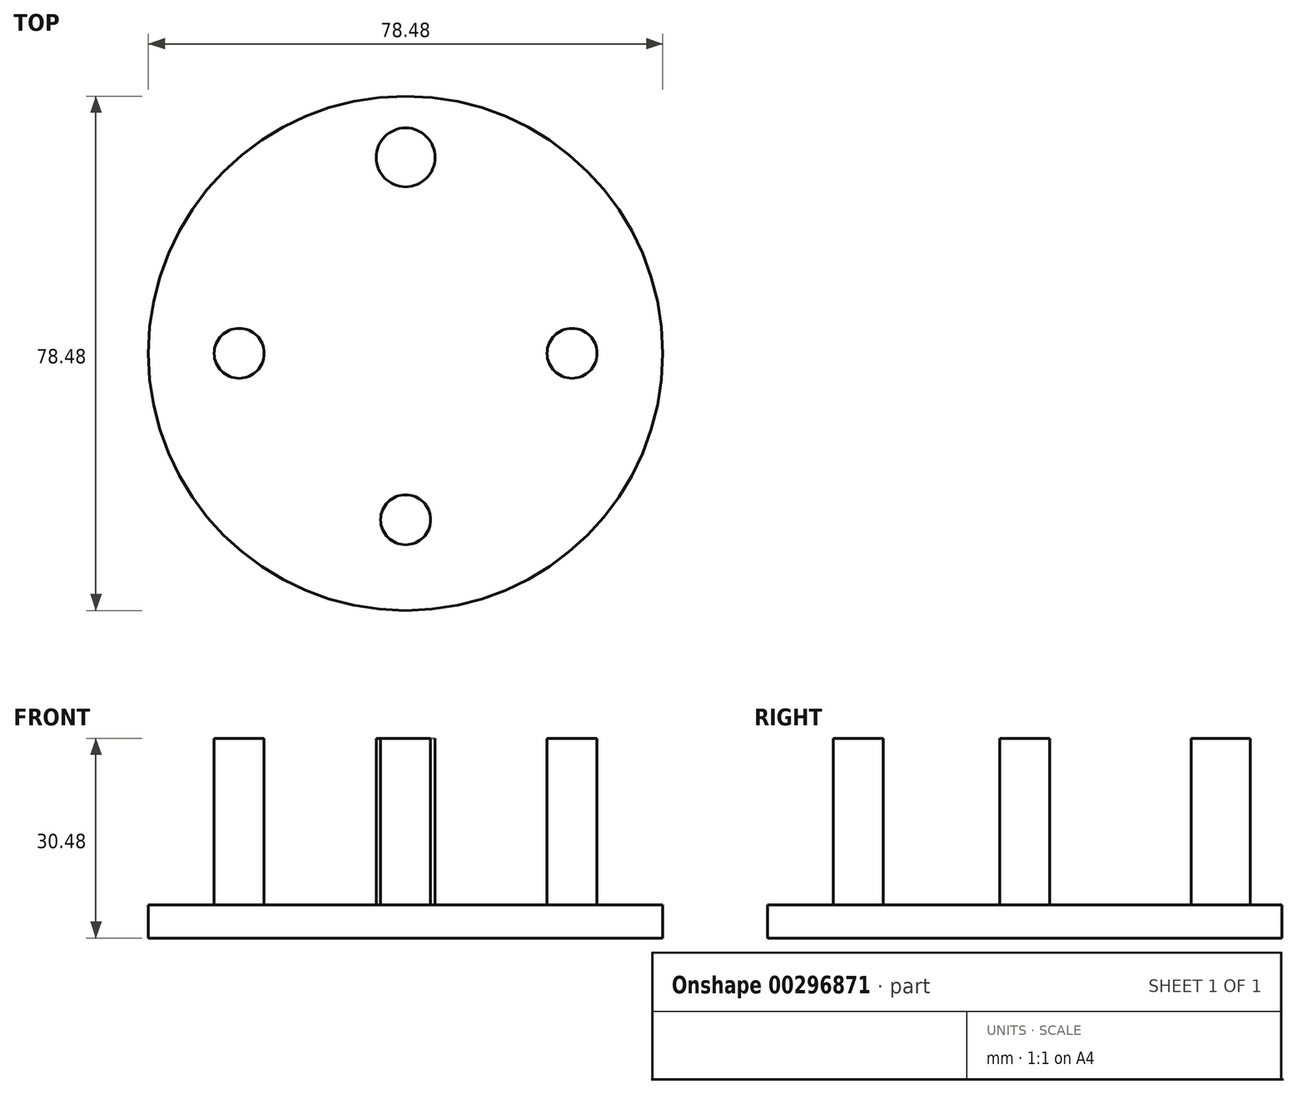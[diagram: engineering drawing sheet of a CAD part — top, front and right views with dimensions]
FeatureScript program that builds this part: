
annotation { "Feature Type Name" : "Feature", "Feature Type Description" : "" }
export const myFeature = defineFeature(function(context is Context, id is Id, definition is map)
    precondition{}
    {
        {
            var Q0;
            Q0=qCreatedBy(makeId("Top.planeOp"),FACE);
            var sketch = newSketch(context, id + "F0", { "sketchPlane" : qUnion([Q0])});
            skCircle(sketch, "E0", {"center": v(0, 0) * mm, "radius": 39.24 * mm});
            skSolve(sketch);
        }
        {
            var Q0;
            Q0=makeQuery(id+"F0.imprint","IMPRINT",FACE,{"disambiguationData":[TD([[makeQuery(id+"F0.imprint","IMPRINT",EDGE,{"derivedFrom":sQuery(id+"F0.wireOp",EDGE,"E0")}),1.0]])]});
            extrude(context, id + "F1", {"entities" : qUnion([Q0]), "depth" : 5.08 * mm});
        }
        {
            var Q0;
            Q0=makeQuery(id+"F1.opExtrude","CAP_FACE",FACE,{"disambiguationData":[OSD([sQuery(id+"F0.wireOp",EDGE,"E0")])],"isStart":false});
            var sketch = newSketch(context, id + "F2", { "sketchPlane" : qUnion([Q0])});
            skCircle(sketch, "E1", {"center": v(0, -25.4) * mm, "radius": 3.81 * mm});
            skCircle(sketch, "E2", {"center": v(0, 29.9) * mm, "radius": 4.5 * mm});
            skSolve(sketch);
        }
        {
            var Q0;
            Q0=makeQuery(id+"F2.imprint","IMPRINT",FACE,{"disambiguationData":[TD([[makeQuery(id+"F2.imprint","IMPRINT",EDGE,{"derivedFrom":sQuery(id+"F2.wireOp",EDGE,"E1")}),-1.0]])]});
            var sketch = newSketch(context, id + "F3", { "sketchPlane" : qUnion([Q0])});
            skCircle(sketch, "E3", {"center": v(-25.4, 0) * mm, "radius": 3.81 * mm});
            skCircle(sketch, "E4", {"center": v(25.4, 0) * mm, "radius": 3.81 * mm});
            skSolve(sketch);
        }
        {
            var Q0;
            Q0=makeQuery(id+"F2.imprint","IMPRINT",FACE,{"disambiguationData":[TD([[makeQuery(id+"F2.imprint","IMPRINT",EDGE,{"derivedFrom":sQuery(id+"F2.wireOp",EDGE,"E2")}),1.0]])]});
            var Q1;
            Q1=makeQuery(id+"F3.imprint","IMPRINT",FACE,{"disambiguationData":[TD([[makeQuery(id+"F3.imprint","IMPRINT",EDGE,{"derivedFrom":sQuery(id+"F3.wireOp",EDGE,"E4")}),1.0]])]});
            var Q2;
            Q2=makeQuery(id+"F3.imprint","IMPRINT",FACE,{"disambiguationData":[TD([[makeQuery(id+"F3.imprint","IMPRINT",EDGE,{"derivedFrom":sQuery(id+"F3.wireOp",EDGE,"E3")}),1.0]])]});
            var Q3;
            Q3=makeQuery(id+"F2.imprint","IMPRINT",FACE,{"disambiguationData":[TD([[makeQuery(id+"F2.imprint","IMPRINT",EDGE,{"derivedFrom":sQuery(id+"F2.wireOp",EDGE,"E1")}),1.0]])]});
            extrude(context, id + "F4", {"entities" : qUnion([Q0, Q1, Q2, Q3]), "operationType" : NewBodyOperationType.ADD, "depth" : 25.4 * mm});
        }
    });
